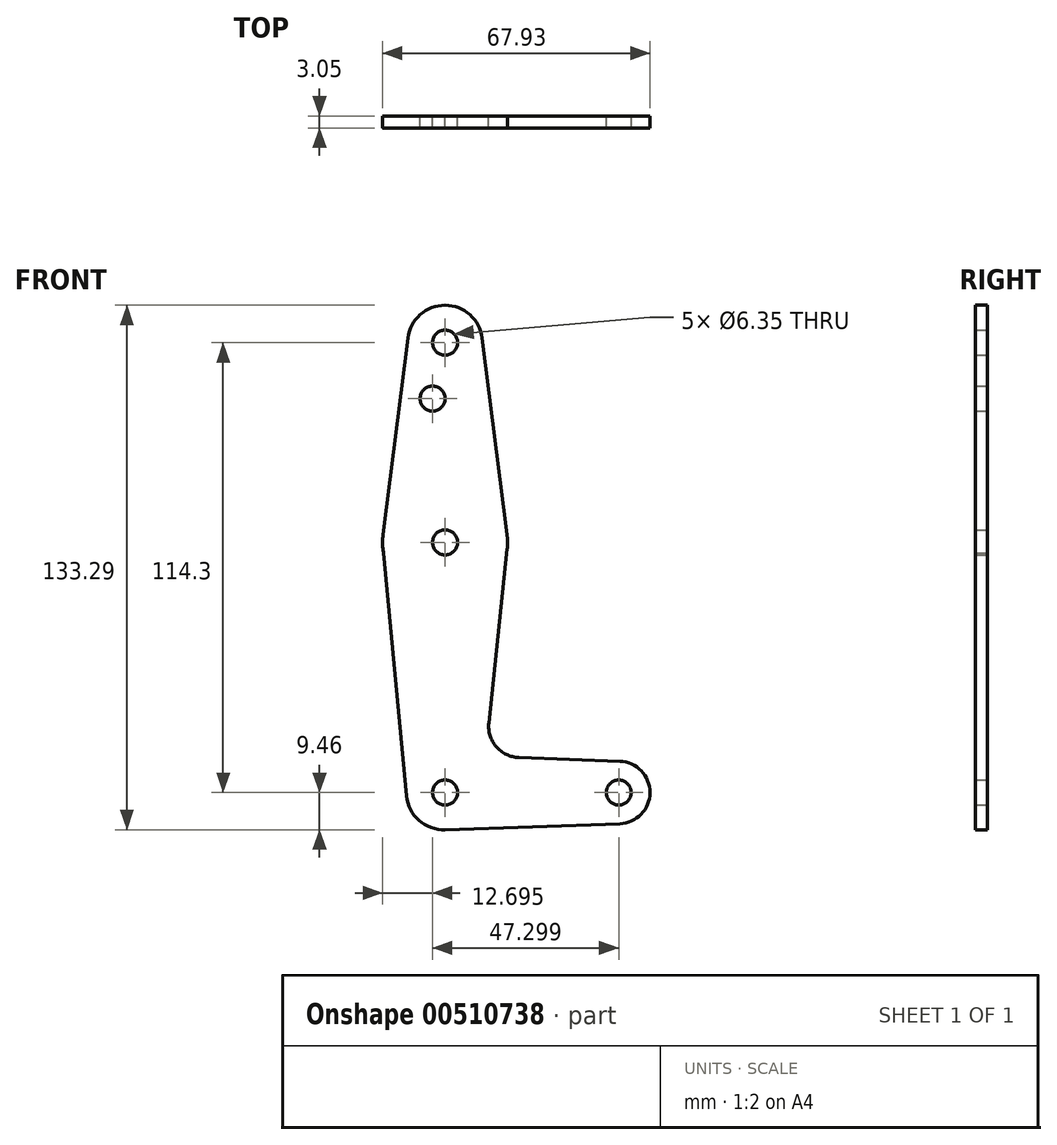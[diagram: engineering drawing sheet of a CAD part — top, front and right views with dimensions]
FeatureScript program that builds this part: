
annotation { "Feature Type Name" : "Feature", "Feature Type Description" : "" }
export const myFeature = defineFeature(function(context is Context, id is Id, definition is map)
    precondition{}
    {
        {
            var Q0;
            Q0=qCreatedBy(makeId("Front.planeOp"),FACE);
            var sketch = newSketch(context, id + "F0", { "sketchPlane" : qUnion([Q0])});
            skLineSegment(sketch, "E0", {"start": v(-0.33, 0.06) * mm, "end": v(44.12, 0) * mm, "construction": true});
            skLineSegment(sketch, "E1", {"start": v(0, 0) * mm, "end": v(0, 114.3) * mm, "construction": true});
            skCircle(sketch, "E2", {"center": v(0, 114.3) * mm, "radius": 9.53 * mm});
            skCircle(sketch, "E3", {"center": v(0, 63.56) * mm, "radius": 15.88 * mm});
            skCircle(sketch, "E4", {"center": v(-0.33, 0.06) * mm, "radius": 9.53 * mm});
            skCircle(sketch, "E5", {"center": v(44.12, 0) * mm, "radius": 7.94 * mm});
            skLineSegment(sketch, "E6", {"start": v(-9.45, 115.5) * mm, "end": v(-15.75, 65.55) * mm});
            skLineSegment(sketch, "E7", {"start": v(9.45, 115.5) * mm, "end": v(15.75, 65.55) * mm});
            skLineSegment(sketch, "E8", {"start": v(-15.64, 60.87) * mm, "end": v(-9.8, -0.83) * mm});
            skLineSegment(sketch, "E9", {"start": v(15.79, 61.9) * mm, "end": v(11.11, 17.67) * mm});
            skLineSegment(sketch, "E10", {"start": v(18.72, 8.89) * mm, "end": v(44.42, 7.93) * mm});
            skLineSegment(sketch, "E11", {"start": v(0, -9.46) * mm, "end": v(44.42, -7.93) * mm});
            skCircle(sketch, "E12", {"center": v(-3.18, 100.09) * mm, "radius": 3.18 * mm});
            skCircle(sketch, "E13", {"center": v(0, 114.3) * mm, "radius": 3.18 * mm});
            skCircle(sketch, "E14", {"center": v(0, 63.56) * mm, "radius": 3.18 * mm});
            skCircle(sketch, "E15", {"center": v(0, 0) * mm, "radius": 3.18 * mm});
            skCircle(sketch, "E16", {"center": v(44.12, 0) * mm, "radius": 3.18 * mm});
            skArc(sketch, "E17.filletArc", {"start": v(11.11, 17.67) * mm, "mid": v(13.01, 11.63) * mm, "end": v(18.72, 8.89) * mm});
            skSolve(sketch);
        }
        {
            var Q0;
            Q0 = qSketchRegion(id + "F0", true);
            extrude(context, id + "F1", {"entities" : qUnion([Q0]), "depth" : 3.05 * mm});
        }
    });
